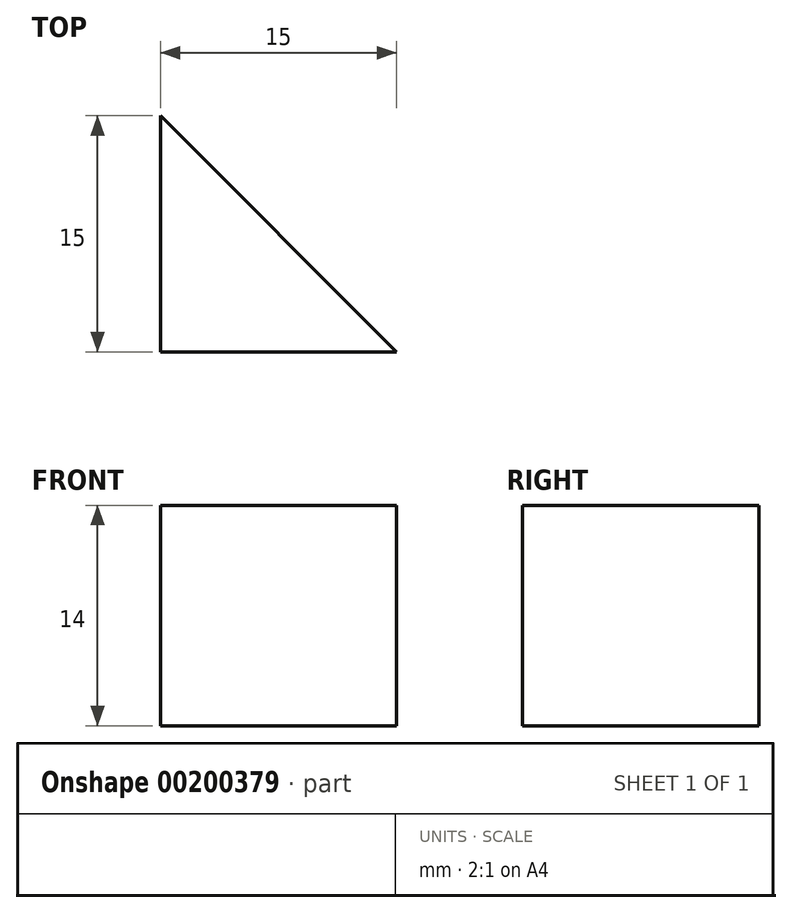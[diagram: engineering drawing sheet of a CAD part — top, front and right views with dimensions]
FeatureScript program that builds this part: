
annotation { "Feature Type Name" : "Feature", "Feature Type Description" : "" }
export const myFeature = defineFeature(function(context is Context, id is Id, definition is map)
    precondition{}
    {
        {
            var Q0;
            Q0=qCreatedBy(makeId("Top.planeOp"),FACE);
            var sketch = newSketch(context, id + "F0", { "sketchPlane" : qUnion([Q0])});
            skLineSegment(sketch, "E0", {"start": v(-37.78, 27.02) * mm, "end": v(-22.78, 27.02) * mm});
            skLineSegment(sketch, "E1", {"start": v(-22.78, 27.02) * mm, "end": v(-37.78, 42.02) * mm});
            skLineSegment(sketch, "E2", {"start": v(-37.78, 42.02) * mm, "end": v(-37.78, 27.02) * mm});
            skSolve(sketch);
        }
        {
            var Q0;
            Q0=makeQuery(id+"F0.imprint","IMPRINT",FACE,{"disambiguationData":[TD([[makeQuery(id+"F0.imprint","IMPRINT",EDGE,{"derivedFrom":sQuery(id+"F0.wireOp",EDGE,"E0")}),1.0]])]});
            extrude(context, id + "F1", {"entities" : qUnion([Q0]), "depth" : 14 * mm});
        }
    });
